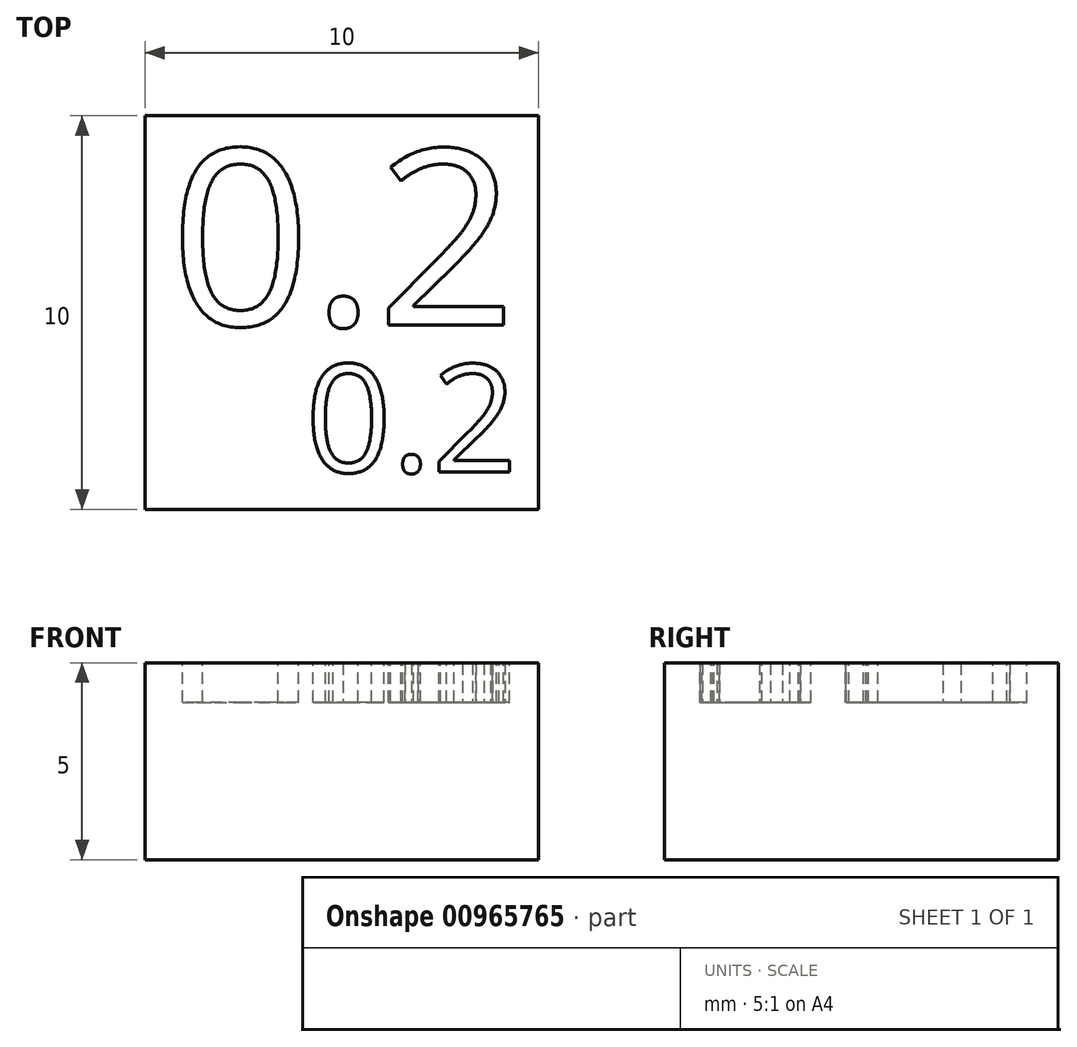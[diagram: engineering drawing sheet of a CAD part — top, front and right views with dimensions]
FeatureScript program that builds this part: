
annotation { "Feature Type Name" : "Feature", "Feature Type Description" : "" }
export const myFeature = defineFeature(function(context is Context, id is Id, definition is map)
    precondition{}
    {
        {
            var Q0;
            Q0=qCreatedBy(makeId("Top.planeOp"),FACE);
            var sketch = newSketch(context, id + "F0", { "sketchPlane" : qUnion([Q0])});
            skLineSegment(sketch, "E0.bottom", {"start": v(5, -5) * mm, "end": v(-5, -5) * mm});
            skLineSegment(sketch, "E0.top", {"start": v(5, 5) * mm, "end": v(-5, 5) * mm});
            skLineSegment(sketch, "E0.left", {"start": v(5, -5) * mm, "end": v(5, 5) * mm});
            skLineSegment(sketch, "E0.right", {"start": v(-5, -5) * mm, "end": v(-5, 5) * mm});
            skSolve(sketch);
        }
        {
            var Q0;
            Q0 = qSketchRegion(id + "F0", true);
            var Q1;
            Q1=makeQuery(id+"F0.imprint","IMPRINT",FACE,{"disambiguationData":[TD([[makeQuery(id+"F0.imprint","IMPRINT",EDGE,{"derivedFrom":sQuery(id+"F0.wireOp",EDGE,"cee0f0d1-9f68-43e3-9c2b-db64f70f2ec6.sketch_text.stroke-8")}),1.0]])]});
            var Q2;
            Q2=makeQuery(id+"F0.imprint","IMPRINT",FACE,{"disambiguationData":[TD([[makeQuery(id+"F0.imprint","IMPRINT",EDGE,{"derivedFrom":sQuery(id+"F0.wireOp",EDGE,"4c9aaef7-7e77-4cad-ac0b-385e3b2ca51a.sketch_text.stroke-8")}),1.0]])]});
            extrude(context, id + "F1", {"entities" : qUnion([Q0, Q1, Q2]), "depth" : 5 * mm, "offsetDistance" : 25 * mm});
        }
        {
            var Q0;
            Q0=makeQuery(id+"F1.opExtrude","CAP_FACE",FACE,{"disambiguationData":[OSD([sQuery(id+"F0.wireOp",EDGE,"E0.bottom"),sQuery(id+"F0.wireOp",EDGE,"E0.top"),sQuery(id+"F0.wireOp",EDGE,"E0.left"),sQuery(id+"F0.wireOp",EDGE,"E0.right")])],"isStart":false});
            var sketch = newSketch(context, id + "F2", { "sketchPlane" : qUnion([Q0])});
            skText(sketch, "E1", { "text": "0.2", "fontName": "OpenSans-Regular.ttf"});
            skText(sketch, "E2", { "text": "0.2\n", "fontName": "OpenSans-Regular.ttf"});
            const initialGuessF2  = {"E1": [-0.00436, -0.00032, 1, 0, 0.0045], "E2": [-0.00092, -0.00405, 1, 0, 0.00275]};
            skSetInitialGuess(sketch, initialGuessF2);
            skSolve(sketch);
        }
        {
            var Q0;
            Q0=makeQuery(id+"F2.imprint","IMPRINT",FACE,{"disambiguationData":[TD([[makeQuery(id+"F2.imprint","IMPRINT",EDGE,{"derivedFrom":sQuery(id+"F2.wireOp",EDGE,"E1.sketch_text.stroke-0")}),-1.0]])]});
            var Q1;
            Q1=makeQuery(id+"F2.imprint","IMPRINT",FACE,{"disambiguationData":[TD([[makeQuery(id+"F2.imprint","IMPRINT",EDGE,{"derivedFrom":sQuery(id+"F2.wireOp",EDGE,"E1.sketch_text.stroke-16")}),-1.0]])]});
            var Q2;
            Q2=makeQuery(id+"F2.imprint","IMPRINT",FACE,{"disambiguationData":[TD([[makeQuery(id+"F2.imprint","IMPRINT",EDGE,{"derivedFrom":sQuery(id+"F2.wireOp",EDGE,"E1.sketch_text.stroke-24")}),-1.0]])]});
            var Q3;
            Q3=makeQuery(id+"F2.imprint","IMPRINT",FACE,{"disambiguationData":[TD([[makeQuery(id+"F2.imprint","IMPRINT",EDGE,{"derivedFrom":sQuery(id+"F2.wireOp",EDGE,"E2.sketch_text.stroke-0")}),-1.0]])]});
            var Q4;
            Q4=makeQuery(id+"F2.imprint","IMPRINT",FACE,{"disambiguationData":[TD([[makeQuery(id+"F2.imprint","IMPRINT",EDGE,{"derivedFrom":sQuery(id+"F2.wireOp",EDGE,"E2.sketch_text.stroke-16")}),-1.0]])]});
            var Q5;
            Q5=makeQuery(id+"F2.imprint","IMPRINT",FACE,{"disambiguationData":[TD([[makeQuery(id+"F2.imprint","IMPRINT",EDGE,{"derivedFrom":sQuery(id+"F2.wireOp",EDGE,"E2.sketch_text.stroke-24")}),-1.0]])]});
            extrude(context, id + "F3", {"entities" : qUnion([Q0, Q1, Q2, Q3, Q4, Q5]), "operationType" : NewBodyOperationType.REMOVE, "oppositeDirection" : true, "depth" : 1 * mm, "offsetDistance" : 25 * mm});
        }
    });
